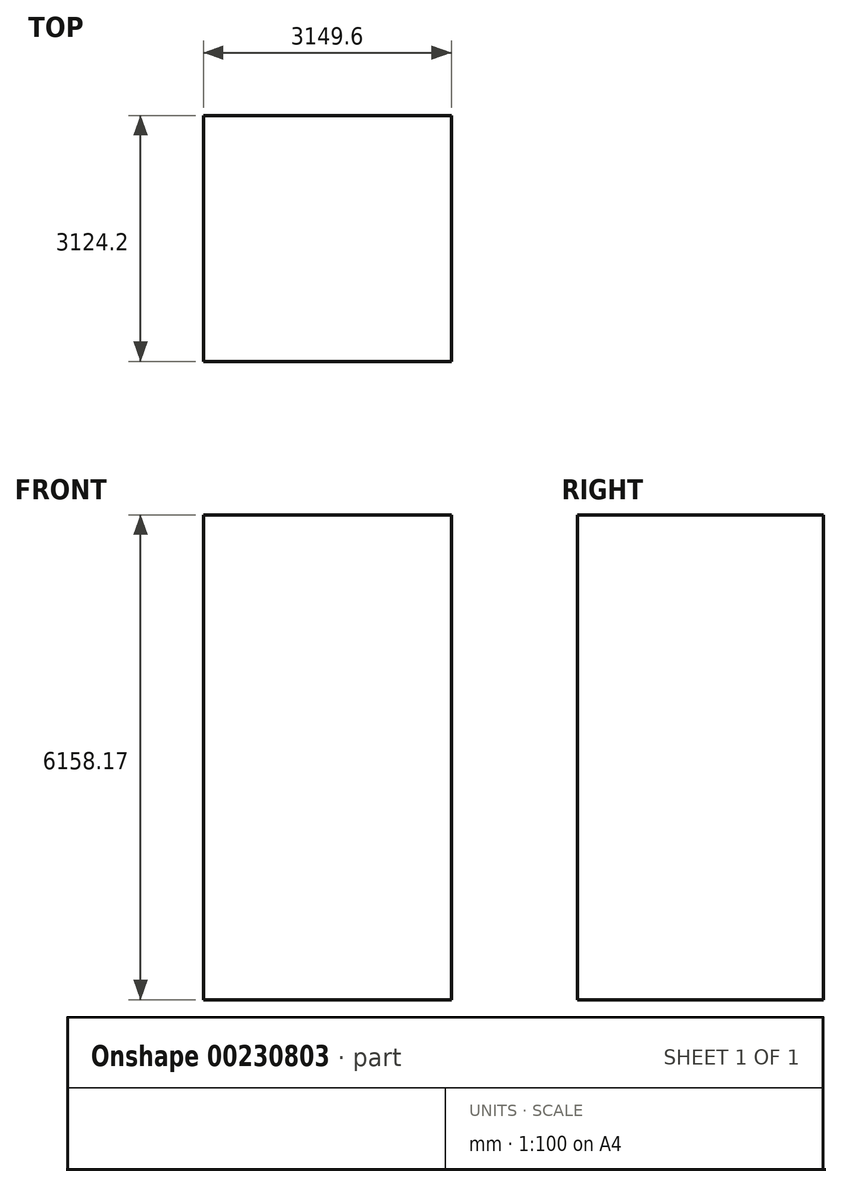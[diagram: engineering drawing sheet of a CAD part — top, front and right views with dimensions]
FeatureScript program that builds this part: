
annotation { "Feature Type Name" : "Feature", "Feature Type Description" : "" }
export const myFeature = defineFeature(function(context is Context, id is Id, definition is map)
    precondition{}
    {
        {
            var Q0;
            Q0=qCreatedBy(makeId("Front.planeOp"),FACE);
            var sketch = newSketch(context, id + "F0", { "sketchPlane" : qUnion([Q0])});
            skLineSegment(sketch, "E0.bottom", {"start": v(-3149.6, 2509.1) * mm, "end": v(0, 2509.1) * mm});
            skLineSegment(sketch, "E0.top", {"start": v(-3149.6, -3649.07) * mm, "end": v(0, -3649.07) * mm});
            skLineSegment(sketch, "E0.left", {"start": v(-3149.6, 2509.1) * mm, "end": v(-3149.6, -3649.07) * mm});
            skLineSegment(sketch, "E0.right", {"start": v(0, 2509.1) * mm, "end": v(0, -3649.07) * mm});
            skSolve(sketch);
        }
        {
            var Q0;
            Q0 = qSketchRegion(id + "F0", true);
            extrude(context, id + "F1", {"entities" : qUnion([Q0]), "depth" : 3124.2 * mm});
        }
    });
